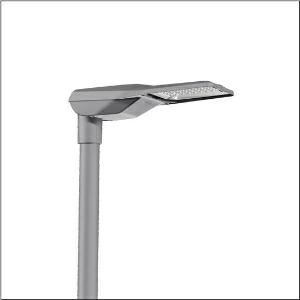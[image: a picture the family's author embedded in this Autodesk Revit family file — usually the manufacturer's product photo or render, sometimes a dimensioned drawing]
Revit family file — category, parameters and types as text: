
# Revit family: streetlight_sl_21_iq_mini___p0_5a_5xe2v31d08gb_51ef
name_source: partatom
category: Lighting Fixtures
units: mm (PartAtom-declared; Revit-internal decimal feet)

## family parameters
Cut with Voids When Loaded = No
Host = Face
Light Source = No
Part Type = Normal
Room Calculation Point = No
Round Connector Dimension = Use Diameter
Shared = No

## types (1)
- --- (1 x LED, 5580 lm, 37.1 W, 3000K)
    Apparent Load = 37 VA
    CIE Flux Codes = 37 73 96 100 100
    Color Rendering = 70
    Color Temperature = 3000K
    Default Elevation = 1800 mm
    Description = Streetlight SL 21 iQ mini, mast luminaire, primary light control with lens, of PMMA, primary optical cover: cover, of toughened safety glass, transparent, light distribution: P0.5a, light emission: direct distribution, primary light characteristic: asymmetric, installation type: post-top, side-entry, LED, High Power LED, rated luminous flux: 5.580lm, luminous efficacy: 150lm/W, light colour: 730, colour temperature: 3000K, control gear: iQ-Comfort, control: pre-setting: linear dimming characteristic, Auto-Match, Temp-Guard, Lumen-Switch, Night-Set, Smart-Wire, Light-Fading, Desk-Remote (wireless, voltage-free reading and setting of iQ features in the workshop via application-optimized NFC function/RFID function), optimised constant luminous flux control (CLO 2.0), mains connection: 220..240V, AC, 50/60Hz, start of lifetime: 37W, end of service life: 39W, reduction: 18W, luminaire housing, of diecast aluminium, powder-coated, SITECO metallic grey (DB 702S), corrosivity category C5 high according to DIN EN ISO 12944, please order mast flange separately, inclination adjustable: 0°, 5°, 10°, 15°, sealing non-destructively replaceable, multi-level sealing system, length: 628mm, width: 235mm, height: 110mm, mast flange for spigot size: 42mm (side-entry): 5XC10008XM4, 60/48mm (side-entry/post-top): 5XC10108XM2, 76/60mm (side-entry/post-top): 5XC10108XM1, mounting height: 4..8m, protection rating (complete): IP66, insulation class (complete): insulation class II (safety insulation), certification: CE, ENEC, ENEC+, VDE, impact resistance: IK10, permissible operating ambient temperature for outdoor applications: -40..+50°C, standard-compliant lighting for roads and squares, packaging unit: 1 piece

Light Distribution: P0.5a
    Height = 110 mm
    Lamp = 1 x LED
    Lamp Light Flux = 5580 lm
    Lamp Power = 37.1 W
    Lamp count = 1
    Length = 625 mm
    Luminous efficacy = 150 lm/W
    Manufacturer = Siteco
    ModVariant = No
    Model = 5XE2V31D08GB
    Mounting Place = Pole
    Mounting Type = Pole top
    Number of Poles = 1
    OnlyDefault = Yes
    Power Factor = 1
    Product Name = Streetlight SL 21 iQ mini | P0.5a
    Product group = mast luminaire | pylon top
    ProductGroupID = 6100
    Protection Class = Protection class II
    Protection Degree = IP 66
    RLX_Detail_Level = 1
    RLX_Emergency_Light_Flux = 0 lm
    RLX_Emergency_Type = 0
    RLX_Emergency_Type_DB = No
    RlxData = <blob elided: 93837 chars, md5=14422170>
    Socket = socket
    Standby Power = 0 W
    System Light Flux = 5580 lm
    System Power = 37 W
    Type Comments = factory setting: luminous flux: 100 % | dim-lin: 254 | 385 mA
    Type Image = l_1003519.jpg
    URL = http://relux.com
    VarID = @adj_079331
    Voltage = 0 V
    Weight = 0.00 kg
    Width = 234 mm

## geometry (parser evidence)
native form markers: Blend x4, Sweep x10
no freeform markers — native parametric forms only
